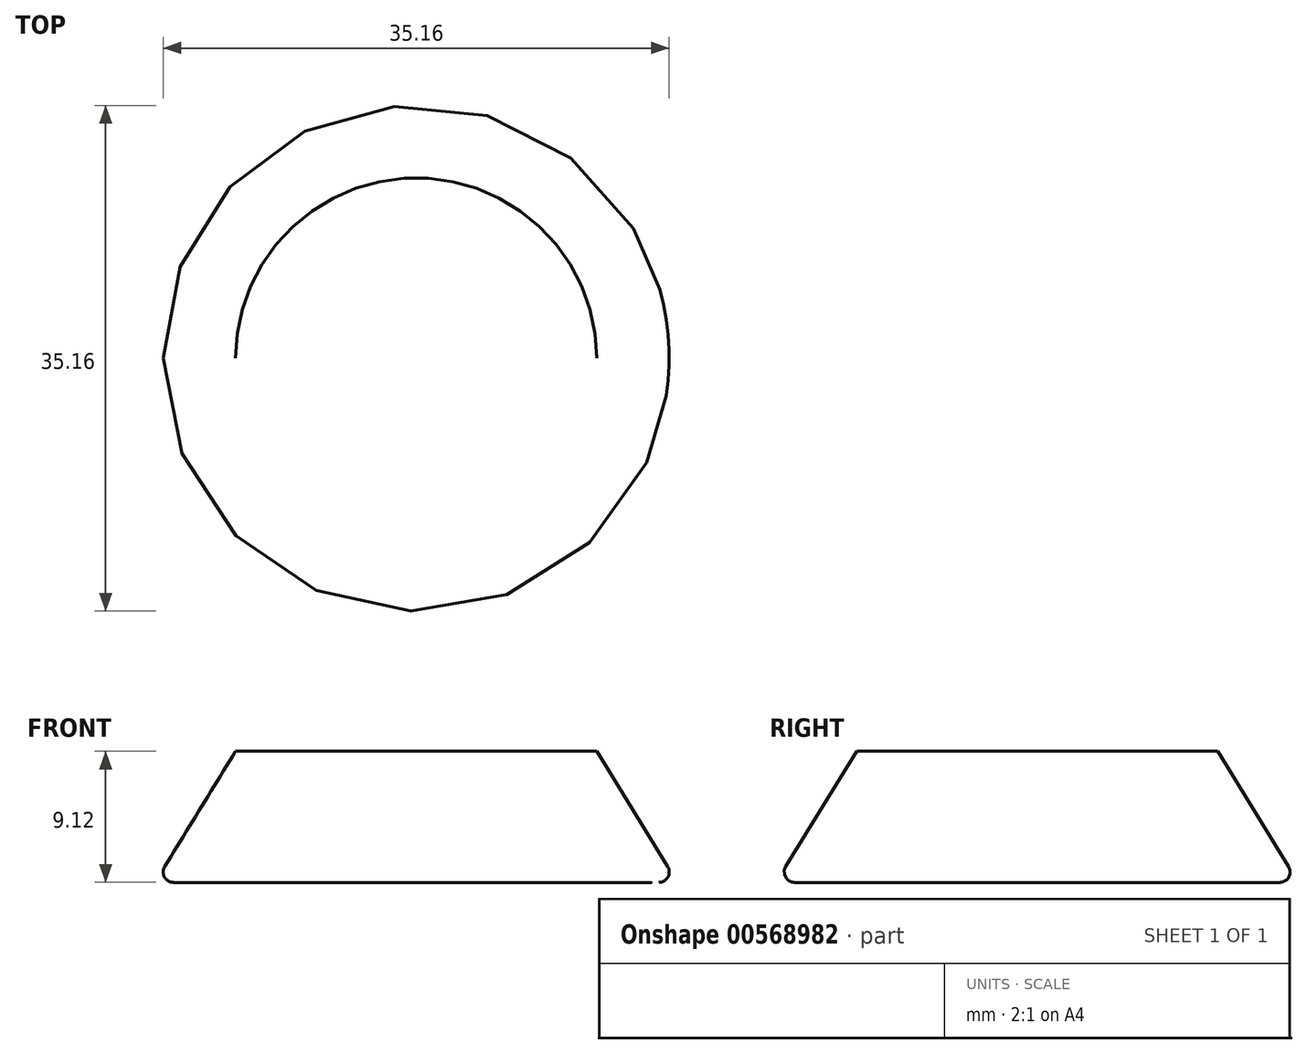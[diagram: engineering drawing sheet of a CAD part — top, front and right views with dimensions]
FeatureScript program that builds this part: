
annotation { "Feature Type Name" : "Feature", "Feature Type Description" : "" }
export const myFeature = defineFeature(function(context is Context, id is Id, definition is map)
    precondition{}
    {
        {
            var Q0;
            Q0=qCreatedBy(makeId("Front.planeOp"),FACE);
            var sketch = newSketch(context, id + "F0", { "sketchPlane" : qUnion([Q0])});
            skLineSegment(sketch, "E0", {"start": v(-18.16, -51.04) * mm, "end": v(18.16, -51.04) * mm});
            skLineSegment(sketch, "E1", {"start": v(-12.54, -41.92) * mm, "end": v(12.54, -41.92) * mm});
            skLineSegment(sketch, "E2", {"start": v(-12.54, -41.92) * mm, "end": v(-18.16, -51.04) * mm});
            skLineSegment(sketch, "E3", {"start": v(12.54, -41.92) * mm, "end": v(18.16, -51.04) * mm});
            skLineSegment(sketch, "E4", {"start": v(0, -41.92) * mm, "end": v(0, -51.04) * mm});
            skSolve(sketch);
        }
        {
            var Q0;
            {var subQ0=sQuery(id+"F0.wireOp",EDGE,"E3");Q0=makeQuery(id+"F0.imprint","IMPRINT",FACE,{"disambiguationData":[TD([[makeQuery(id+"F0.imprint","IMPRINT",EDGE,{"derivedFrom":subQ0}),-1.0]])]});}
            var Q1;
            Q1=sQuery(id+"F0.wireOp",EDGE,"E4");
            revolve(context, id + "F1", {"entities" : qUnion([Q0]), "axis" : qUnion([Q1]), "revolveType" : RevolveType.FULL});
        }
        {
            var Q0;
            Q0=makeQuery(id+"F1.opRevolve","SWEPT_EDGE",EDGE,{"disambiguationData":[OSD([sQuery(id+"F0.wireOp",EDGE,"E0"),sQuery(id+"F0.wireOp",EDGE,"E3")])]});
            fillet(context, id + "F2", {"entities" : qUnion([Q0]), "radius" : 0.73 * mm, "tangentPropagation" : true, "allowEdgeOverflow" : false});
        }
    });
